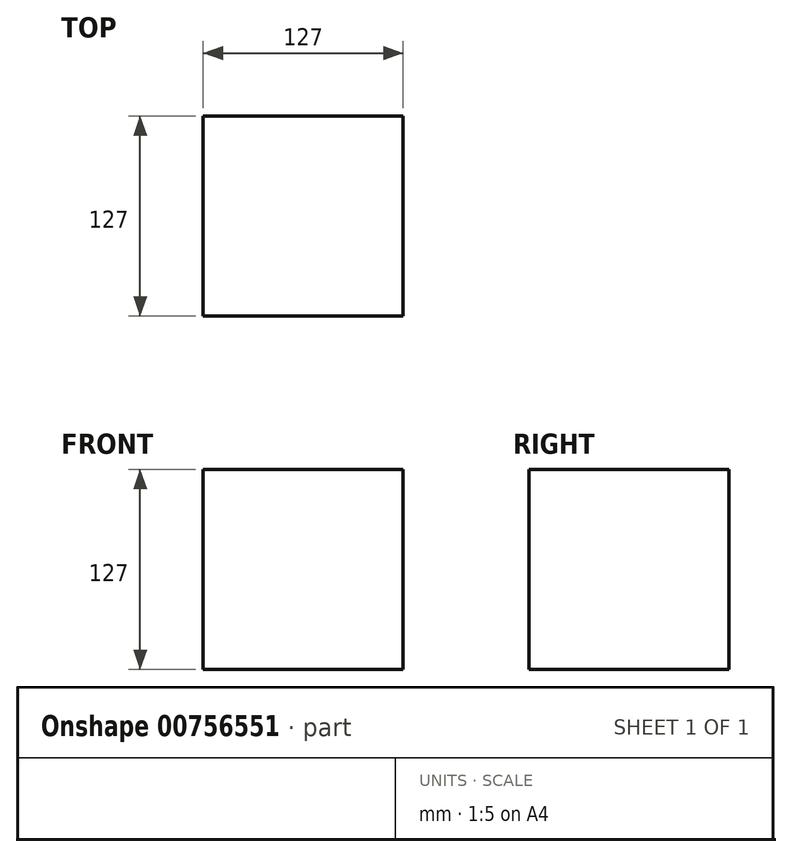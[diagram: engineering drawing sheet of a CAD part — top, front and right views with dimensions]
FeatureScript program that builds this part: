
annotation { "Feature Type Name" : "Feature", "Feature Type Description" : "" }
export const myFeature = defineFeature(function(context is Context, id is Id, definition is map)
    precondition{}
    {
        {
            var Q0;
            Q0=qCreatedBy(makeId("Right.planeOp"),FACE);
            var sketch = newSketch(context, id + "F0", { "sketchPlane" : qUnion([Q0])});
            skLineSegment(sketch, "E0.bottom", {"start": v(-63.5, 63.5) * mm, "end": v(63.5, 63.5) * mm});
            skLineSegment(sketch, "E0.top", {"start": v(-63.5, -63.5) * mm, "end": v(63.5, -63.5) * mm});
            skLineSegment(sketch, "E0.left", {"start": v(-63.5, 63.5) * mm, "end": v(-63.5, -63.5) * mm});
            skLineSegment(sketch, "E0.right", {"start": v(63.5, 63.5) * mm, "end": v(63.5, -63.5) * mm});
            skPoint(sketch, "E0.middle", {"position": v(0, 0) * mm});
            skCircle(sketch, "E1", {"center": v(0, 0) * mm, "radius": 63.5 * mm});
            skSolve(sketch);
        }
        {
            var Q0;
            {var subQ0=sQuery(id+"F0.wireOp",EDGE,"E0.right");var subQ1=sQuery(id+"F0.wireOp",EDGE,"E0.bottom");var subQ2=makeQuery(id+"F0.imprint","INTERSECT",VERTEX,{"derivedFrom":[subQ1,subQ0]});Q0=makeQuery(id+"F0.imprint","IMPRINT",FACE,{"disambiguationData":[TD([[makeQuery(id+"F0.imprint","IMPRINT",EDGE,{"disambiguationData":[TD([[subQ2,1.0]])],"derivedFrom":subQ1}),-1.0]])]});}
            var Q1;
            {var subQ0=sQuery(id+"F0.wireOp",EDGE,"E0.left");var subQ1=sQuery(id+"F0.wireOp",EDGE,"E0.bottom");var subQ2=makeQuery(id+"F0.imprint","INTERSECT",VERTEX,{"derivedFrom":[subQ1,subQ0]});Q1=makeQuery(id+"F0.imprint","IMPRINT",FACE,{"disambiguationData":[TD([[makeQuery(id+"F0.imprint","IMPRINT",EDGE,{"disambiguationData":[TD([[subQ2,-1.0]])],"derivedFrom":subQ1}),-1.0]])]});}
            var Q2;
            {var subQ0=sQuery(id+"F0.wireOp",EDGE,"E0.left");var subQ1=sQuery(id+"F0.wireOp",EDGE,"E0.top");var subQ2=makeQuery(id+"F0.imprint","INTERSECT",VERTEX,{"derivedFrom":[subQ1,subQ0]});Q2=makeQuery(id+"F0.imprint","IMPRINT",FACE,{"disambiguationData":[TD([[makeQuery(id+"F0.imprint","IMPRINT",EDGE,{"disambiguationData":[TD([[subQ2,-1.0]])],"derivedFrom":subQ1}),1.0]])]});}
            var Q3;
            {var subQ0=sQuery(id+"F0.wireOp",EDGE,"E0.right");var subQ1=sQuery(id+"F0.wireOp",EDGE,"E0.top");var subQ2=makeQuery(id+"F0.imprint","INTERSECT",VERTEX,{"derivedFrom":[subQ1,subQ0]});Q3=makeQuery(id+"F0.imprint","IMPRINT",FACE,{"disambiguationData":[TD([[makeQuery(id+"F0.imprint","IMPRINT",EDGE,{"disambiguationData":[TD([[subQ2,1.0]])],"derivedFrom":subQ1}),1.0]])]});}
            var Q4;
            {var subQ0=sQuery(id+"F0.wireOp",EDGE,"E1");var subQ1=makeQuery(id+"F0.imprint","INTERSECT",VERTEX,{"derivedFrom":[sQuery(id+"F0.wireOp",EDGE,"E0.bottom"),subQ0]});Q4=makeQuery(id+"F0.imprint","IMPRINT",FACE,{"disambiguationData":[TD([[makeQuery(id+"F0.imprint","IMPRINT",EDGE,{"disambiguationData":[TD([[subQ1,1.0]])],"derivedFrom":subQ0}),1.0]])]});}
            extrude(context, id + "F1", {"entities" : qUnion([Q0, Q1, Q2, Q3, Q4]), "depth" : 127 * mm, "offsetDistance" : 25.4 * mm});
        }
    });
